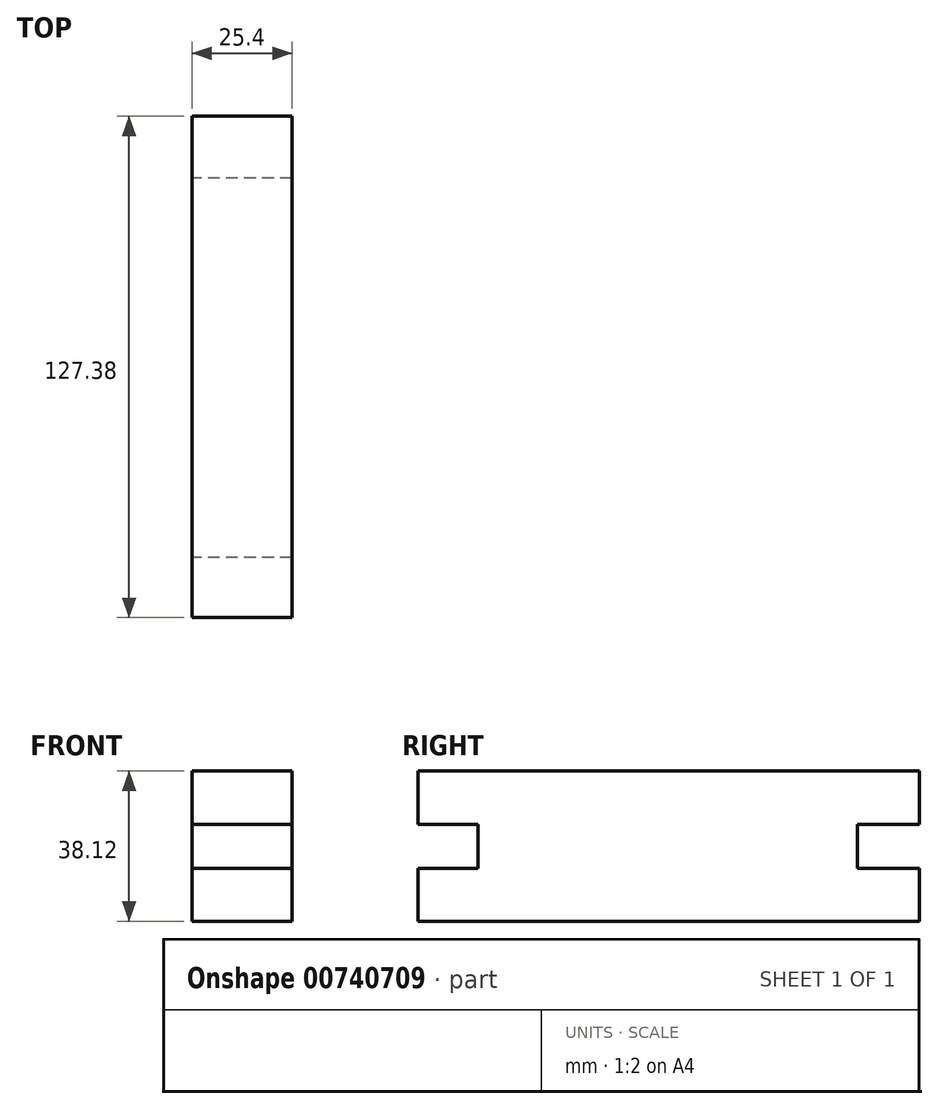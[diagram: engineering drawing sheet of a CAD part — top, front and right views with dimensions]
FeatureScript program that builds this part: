
annotation { "Feature Type Name" : "Feature", "Feature Type Description" : "" }
export const myFeature = defineFeature(function(context is Context, id is Id, definition is map)
    precondition{}
    {
        {
            var Q0;
            Q0=qCreatedBy(makeId("Right.planeOp"),FACE);
            var sketch = newSketch(context, id + "F0", { "sketchPlane" : qUnion([Q0])});
            skLineSegment(sketch, "E0", {"start": v(-62.66, 29.68) * mm, "end": v(-47.37, 29.68) * mm});
            skLineSegment(sketch, "E1", {"start": v(-47.37, 18.5) * mm, "end": v(-62.66, 18.5) * mm});
            skLineSegment(sketch, "E2", {"start": v(-62.66, 29.68) * mm, "end": v(-62.66, 43.14) * mm});
            skLineSegment(sketch, "E3", {"start": v(-62.66, 18.5) * mm, "end": v(-62.66, 5.02) * mm});
            skLineSegment(sketch, "E4", {"start": v(-62.66, 5.02) * mm, "end": v(64.72, 5.02) * mm});
            skLineSegment(sketch, "E5", {"start": v(64.72, 5.02) * mm, "end": v(64.72, 18.5) * mm});
            skLineSegment(sketch, "E6", {"start": v(64.72, 18.5) * mm, "end": v(48.96, 18.5) * mm});
            skLineSegment(sketch, "E7", {"start": v(-47.37, 29.68) * mm, "end": v(-47.37, 18.5) * mm});
            skLineSegment(sketch, "E8", {"start": v(48.96, 18.5) * mm, "end": v(48.96, 29.68) * mm});
            skLineSegment(sketch, "E9", {"start": v(48.96, 29.68) * mm, "end": v(64.72, 29.68) * mm});
            skLineSegment(sketch, "E10", {"start": v(64.72, 29.68) * mm, "end": v(64.72, 43.14) * mm});
            skLineSegment(sketch, "E11", {"start": v(64.72, 43.14) * mm, "end": v(-62.66, 43.14) * mm});
            skSolve(sketch);
        }
        {
            var Q0;
            Q0=makeQuery(id+"F0.imprint","IMPRINT",FACE,{"disambiguationData":[TD([[makeQuery(id+"F0.imprint","IMPRINT",EDGE,{"derivedFrom":sQuery(id+"F0.wireOp",EDGE,"E0")}),1.0]])]});
            extrude(context, id + "F1", {"entities" : qUnion([Q0]), "depth" : 25.4 * mm, "offsetDistance" : 25.4 * mm});
        }
    });
